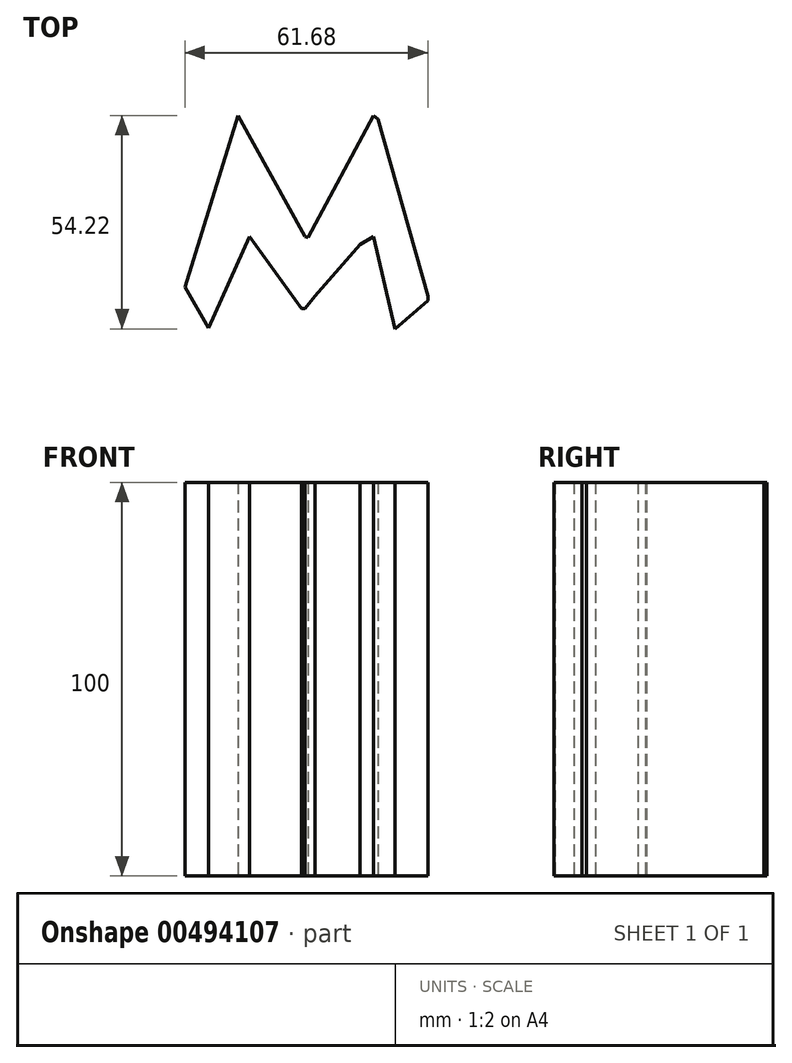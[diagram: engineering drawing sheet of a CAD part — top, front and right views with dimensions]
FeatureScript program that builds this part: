
annotation { "Feature Type Name" : "Feature", "Feature Type Description" : "" }
export const myFeature = defineFeature(function(context is Context, id is Id, definition is map)
    precondition{}
    {
        {
            var Q0;
            Q0=qCreatedBy(makeId("Top.planeOp"),FACE);
            var sketch = newSketch(context, id + "F0", { "sketchPlane" : qUnion([Q0])});
            skLineSegment(sketch, "E0", {"start": v(-40.74, -23.67) * mm, "end": v(-27.25, 19.94) * mm});
            skLineSegment(sketch, "E1", {"start": v(-27.25, 19.94) * mm, "end": v(-10.2, -10.76) * mm});
            skLineSegment(sketch, "E2", {"start": v(-9.54, -11.03) * mm, "end": v(7.17, 19.94) * mm});
            skLineSegment(sketch, "E3", {"start": v(8.32, 19.08) * mm, "end": v(20.94, -25.96) * mm});
            skLineSegment(sketch, "E4", {"start": v(20.94, -27.11) * mm, "end": v(12.62, -34.28) * mm});
            skLineSegment(sketch, "E5", {"start": v(12.62, -34.28) * mm, "end": v(7.17, -10.76) * mm});
            skLineSegment(sketch, "E6", {"start": v(3.7, -12.85) * mm, "end": v(-7.75, -25.96) * mm});
            skLineSegment(sketch, "E7", {"start": v(-7.75, -25.96) * mm, "end": v(-10.2, -29.11) * mm});
            skLineSegment(sketch, "E8", {"start": v(-11.19, -29.12) * mm, "end": v(-24.39, -10.76) * mm});
            skLineSegment(sketch, "E9", {"start": v(-24.39, -10.76) * mm, "end": v(-34.71, -34) * mm});
            skLineSegment(sketch, "E10", {"start": v(-40.74, -23.67) * mm, "end": v(-34.71, -34) * mm});
            skLineSegment(sketch, "E11", {"start": v(20.94, -27.11) * mm, "end": v(20.94, -25.96) * mm});
            skLineSegment(sketch, "E12", {"start": v(-11.19, -29.12) * mm, "end": v(-10.2, -29.11) * mm});
            skLineSegment(sketch, "E13", {"start": v(7.17, -10.76) * mm, "end": v(3.7, -12.85) * mm});
            skLineSegment(sketch, "E14", {"start": v(-9.54, -11.03) * mm, "end": v(-10.2, -10.76) * mm});
            skLineSegment(sketch, "E15", {"start": v(7.17, -10.76) * mm, "end": v(7.66, -12.85) * mm});
            skLineSegment(sketch, "E16", {"start": v(8.32, 19.08) * mm, "end": v(7.17, 19.94) * mm});
            skSolve(sketch);
        }
        {
            var Q0;
            Q0 = qSketchRegion(id + "F0", true);
            extrude(context, id + "F1", {"entities" : qUnion([Q0]), "depth" : 100 * mm});
        }
    });
